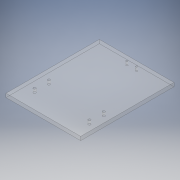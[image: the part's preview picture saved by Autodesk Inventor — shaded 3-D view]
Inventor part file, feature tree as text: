
AUTODESK INVENTOR PART (.ipt)
format: ipt  version: 2018 (Build 220112000, 112)  size: 126,976 bytes
history: native  units: in
note: dims shown in document units (in); Inventor stores cm internally (conversion verified against a paired STEP export)
features: sketch x3, hole x2, sheet_metal_op x1, other x1
ambient origin geometry x8: Origin, YZ Plane, XZ Plane, XY Plane, X Axis, Y Axis, Z Axis, Center Point
bodies: Solid1 (feature_tree)
feature tree (7):
  sheet_metal_op  "Face1"
  hole  "Hole1"  [1 undecoded]
  hole  "Hole2"  [1 undecoded]
  sketch  "Sketch1"  dims[d0=4.0in d1=5.0in]
  other  "Plate1"
  sketch  "Sketch2"  dims[d4=0.2in d5=0.77in]
  sketch  "Sketch3"  dims[d6=0.53in d7=0.129in d8=0.75in d9=0.279in d10=0.188in d11=0.5635in d12=0.2in d13=0.8108in d14=1.0in d15=1.0in d16=0.52in d17=0.09in d18=0.5in d19=0.375in d20=0.25in d21=0.5635in d22=0.2in d23=0.8108in]
note: 2 required parameter values undecoded (feature->parameter linkage not recoverable at this tier; creation-order binding heuristic only, values carry confidence <= 0.55)
